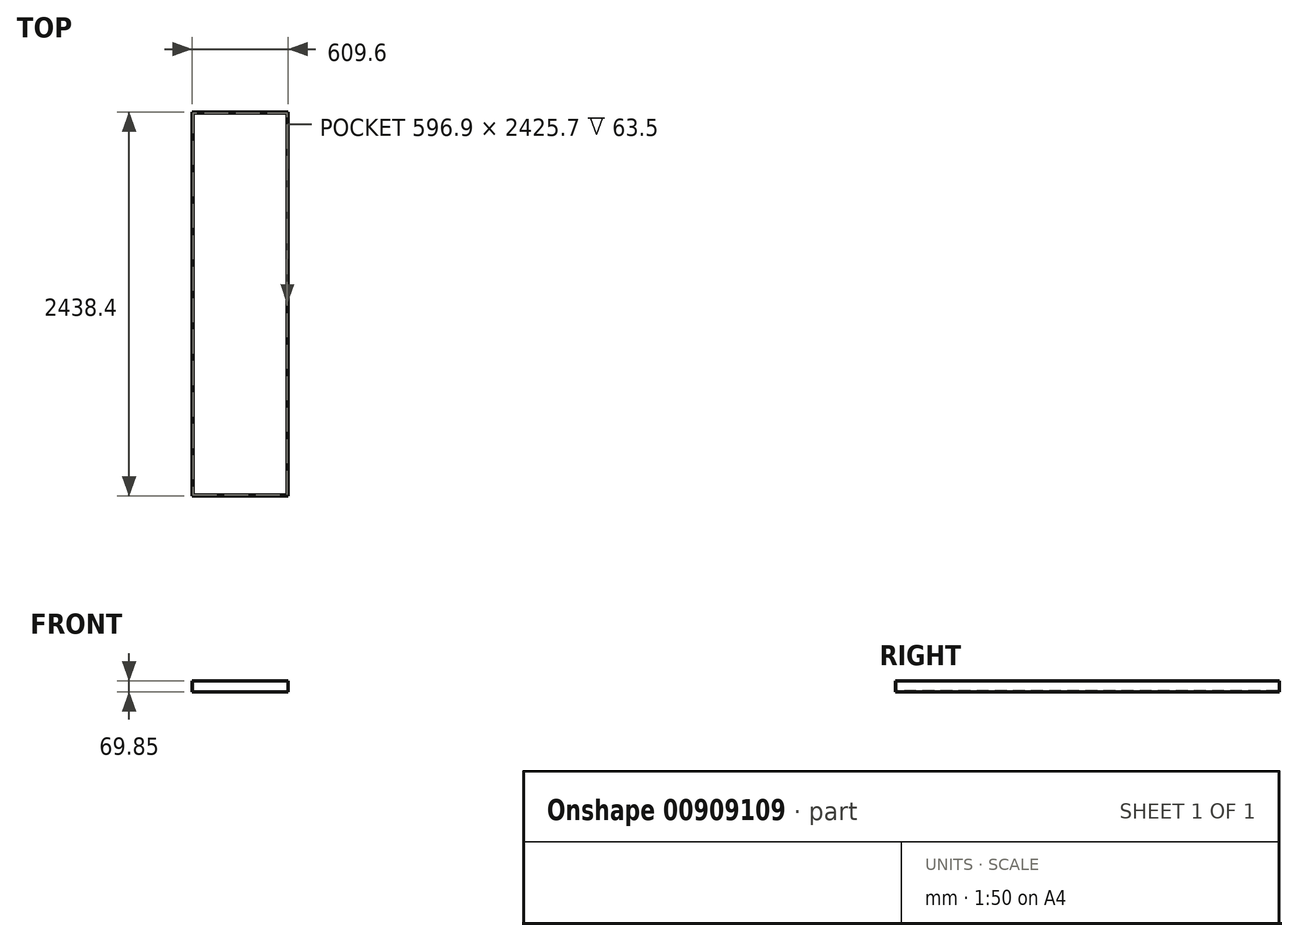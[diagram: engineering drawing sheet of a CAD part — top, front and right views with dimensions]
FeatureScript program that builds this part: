
annotation { "Feature Type Name" : "Feature", "Feature Type Description" : "" }
export const myFeature = defineFeature(function(context is Context, id is Id, definition is map)
    precondition{}
    {
        {
            var Q0;
            Q0=qCreatedBy(makeId("Top.planeOp"),FACE);
            var sketch = newSketch(context, id + "F0", { "sketchPlane" : qUnion([Q0])});
            skLineSegment(sketch, "E0.bottom", {"start": v(-305.28, 2108.07) * mm, "end": v(304.32, 2108.07) * mm});
            skLineSegment(sketch, "E0.top", {"start": v(-305.28, -330.33) * mm, "end": v(304.32, -330.33) * mm});
            skLineSegment(sketch, "E0.left", {"start": v(-305.28, 2108.07) * mm, "end": v(-305.28, -330.33) * mm});
            skLineSegment(sketch, "E0.right", {"start": v(304.32, 2108.07) * mm, "end": v(304.32, -330.33) * mm});
            skSolve(sketch);
        }
        {
            var Q0;
            Q0 = qSketchRegion(id + "F0", true);
            extrude(context, id + "F1", {"entities" : qUnion([Q0]), "depth" : 6.35 * mm, "offsetDistance" : 25.4 * mm});
        }
        {
            var Q0;
            Q0=makeQuery(id+"F1.opExtrude","CAP_FACE",FACE,{"disambiguationData":[OSD([sQuery(id+"F0.wireOp",EDGE,"E0.bottom"),sQuery(id+"F0.wireOp",EDGE,"E0.top"),sQuery(id+"F0.wireOp",EDGE,"E0.left"),sQuery(id+"F0.wireOp",EDGE,"E0.right")])],"isStart":false});
            var sketch = newSketch(context, id + "F2", { "sketchPlane" : qUnion([Q0])});
            skLineSegment(sketch, "E1.bottom", {"start": v(-305.28, 2108.07) * mm, "end": v(304.32, 2108.07) * mm});
            skLineSegment(sketch, "E1.top", {"start": v(-305.28, 2101.72) * mm, "end": v(304.32, 2101.72) * mm});
            skLineSegment(sketch, "E1.left", {"start": v(-305.28, 2108.07) * mm, "end": v(-305.28, 2101.72) * mm});
            skLineSegment(sketch, "E1.right", {"start": v(304.32, 2108.07) * mm, "end": v(304.32, 2101.72) * mm});
            skSolve(sketch);
        }
        {
            var Q0;
            Q0 = qSketchRegion(id + "F2", true);
            extrude(context, id + "F3", {"entities" : qUnion([Q0]), "operationType" : NewBodyOperationType.ADD, "depth" : 63.5 * mm, "offsetDistance" : 25.4 * mm});
        }
        {
            var Q0;
            Q0=makeQuery(id+"F1.opExtrude","CAP_FACE",FACE,{"disambiguationData":[OSD([sQuery(id+"F0.wireOp",EDGE,"E0.bottom"),sQuery(id+"F0.wireOp",EDGE,"E0.top"),sQuery(id+"F0.wireOp",EDGE,"E0.left"),sQuery(id+"F0.wireOp",EDGE,"E0.right")])],"isStart":false});
            var sketch = newSketch(context, id + "F4", { "sketchPlane" : qUnion([Q0])});
            skLineSegment(sketch, "E2.bottom", {"start": v(-305.28, -330.33) * mm, "end": v(304.32, -330.33) * mm});
            skLineSegment(sketch, "E2.top", {"start": v(-305.28, -323.98) * mm, "end": v(304.32, -323.98) * mm});
            skLineSegment(sketch, "E2.left", {"start": v(-305.28, -330.33) * mm, "end": v(-305.28, -323.98) * mm});
            skLineSegment(sketch, "E2.right", {"start": v(304.32, -330.33) * mm, "end": v(304.32, -323.98) * mm});
            skSolve(sketch);
        }
        {
            var Q0;
            Q0 = qSketchRegion(id + "F4", true);
            extrude(context, id + "F5", {"entities" : qUnion([Q0]), "operationType" : NewBodyOperationType.ADD, "depth" : 63.5 * mm, "offsetDistance" : 25.4 * mm});
        }
        {
            var Q0;
            Q0=makeQuery(id+"F1.opExtrude","CAP_FACE",FACE,{"disambiguationData":[OSD([sQuery(id+"F0.wireOp",EDGE,"E0.bottom"),sQuery(id+"F0.wireOp",EDGE,"E0.top"),sQuery(id+"F0.wireOp",EDGE,"E0.left"),sQuery(id+"F0.wireOp",EDGE,"E0.right")])],"isStart":false});
            var sketch = newSketch(context, id + "F6", { "sketchPlane" : qUnion([Q0])});
            skLineSegment(sketch, "E3.bottom", {"start": v(-305.28, 2101.72) * mm, "end": v(-298.93, 2101.72) * mm});
            skLineSegment(sketch, "E3.top", {"start": v(-305.28, -323.98) * mm, "end": v(-298.93, -323.98) * mm});
            skLineSegment(sketch, "E3.left", {"start": v(-305.28, 2101.72) * mm, "end": v(-305.28, -323.98) * mm});
            skLineSegment(sketch, "E3.right", {"start": v(-298.93, 2101.72) * mm, "end": v(-298.93, -323.98) * mm});
            skSolve(sketch);
        }
        {
            var Q0;
            Q0 = qSketchRegion(id + "F6", true);
            extrude(context, id + "F7", {"entities" : qUnion([Q0]), "operationType" : NewBodyOperationType.ADD, "depth" : 63.5 * mm, "offsetDistance" : 25.4 * mm});
        }
        {
            var Q0;
            Q0=makeQuery(id+"F1.opExtrude","CAP_FACE",FACE,{"disambiguationData":[OSD([sQuery(id+"F0.wireOp",EDGE,"E0.bottom"),sQuery(id+"F0.wireOp",EDGE,"E0.top"),sQuery(id+"F0.wireOp",EDGE,"E0.left"),sQuery(id+"F0.wireOp",EDGE,"E0.right")])],"isStart":false});
            var sketch = newSketch(context, id + "F8", { "sketchPlane" : qUnion([Q0])});
            skLineSegment(sketch, "E4.bottom", {"start": v(304.32, 2101.72) * mm, "end": v(297.97, 2101.72) * mm});
            skLineSegment(sketch, "E4.top", {"start": v(304.32, -323.98) * mm, "end": v(297.97, -323.98) * mm});
            skLineSegment(sketch, "E4.left", {"start": v(304.32, 2101.72) * mm, "end": v(304.32, -323.98) * mm});
            skLineSegment(sketch, "E4.right", {"start": v(297.97, 2101.72) * mm, "end": v(297.97, -323.98) * mm});
            skSolve(sketch);
        }
        {
            var Q0;
            Q0 = qSketchRegion(id + "F8", true);
            extrude(context, id + "F9", {"entities" : qUnion([Q0]), "operationType" : NewBodyOperationType.ADD, "depth" : 63.5 * mm, "offsetDistance" : 25.4 * mm});
        }
    });
